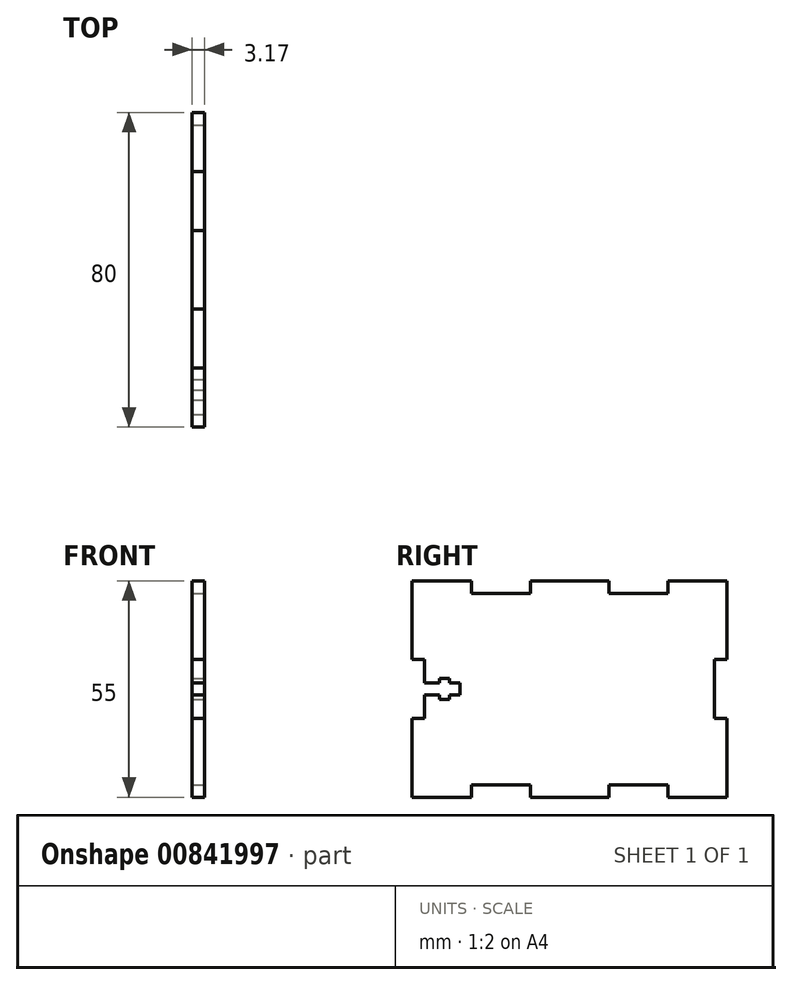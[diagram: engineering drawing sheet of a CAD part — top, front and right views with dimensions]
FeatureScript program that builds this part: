
annotation { "Feature Type Name" : "Feature", "Feature Type Description" : "" }
export const myFeature = defineFeature(function(context is Context, id is Id, definition is map)
    precondition{}
    {
        {
            assignVariable(context, id + "F0", {"name" : "mat_t", "anyValue" : 3.17});
        }
        {
            var Q0;
            Q0=qCreatedBy(makeId("Right.planeOp"),FACE);
            var sketch = newSketch(context, id + "F1", { "sketchPlane" : qUnion([Q0])});
            skLineSegment(sketch, "E0.bottom", {"start": v(40, -27.5) * mm, "end": v(-40, -27.5) * mm});
            skLineSegment(sketch, "E0.top", {"start": v(40, 27.5) * mm, "end": v(-40, 27.5) * mm});
            skLineSegment(sketch, "E0.left", {"start": v(40, -27.5) * mm, "end": v(40, 27.5) * mm});
            skLineSegment(sketch, "E0.right", {"start": v(-40, -27.5) * mm, "end": v(-40, 27.5) * mm});
            skPoint(sketch, "E0.middle", {"position": v(0, 0) * mm});
            skSolve(sketch);
        }
        {
            var Q0;
            Q0 = qSketchRegion(id + "F1", true);
            extrude(context, id + "F2", {"entities" : qUnion([Q0]), "depth" : (getVariable(context, 'mat_t')) * mm, "offsetDistance" : 25 * mm});
        }
        {
            var Q0;
            Q0=makeQuery(id+"F2.opExtrude","CAP_FACE",FACE,{"disambiguationData":[OSD([sQuery(id+"F1.wireOp",EDGE,"E0.bottom"),sQuery(id+"F1.wireOp",EDGE,"E0.top"),sQuery(id+"F1.wireOp",EDGE,"E0.left"),sQuery(id+"F1.wireOp",EDGE,"E0.right")])],"isStart":false});
            var sketch = newSketch(context, id + "F3", { "sketchPlane" : qUnion([Q0])});
            skLineSegment(sketch, "E1", {"start": v(0, 27.5) * mm, "end": v(0, -27.5) * mm, "construction": true});
            skLineSegment(sketch, "E2.bottom", {"start": v(40, 7.5) * mm, "end": v(36.83, 7.5) * mm});
            skLineSegment(sketch, "E2.top", {"start": v(40, -7.5) * mm, "end": v(36.83, -7.5) * mm});
            skLineSegment(sketch, "E2.left", {"start": v(40, 7.5) * mm, "end": v(40, -7.5) * mm});
            skLineSegment(sketch, "E2.right", {"start": v(36.83, 7.5) * mm, "end": v(36.83, -7.5) * mm});
            skPoint(sketch, "E3", {"position": v(40, 0) * mm});
            skLineSegment(sketch, "E4", {"start": v(-40, 0) * mm, "end": v(40, 0) * mm, "construction": true});
            skLineSegment(sketch, "E5.bottom", {"start": v(-25, -27.5) * mm, "end": v(-10, -27.5) * mm});
            skLineSegment(sketch, "E5.top", {"start": v(-25, -24.32) * mm, "end": v(-10, -24.32) * mm});
            skLineSegment(sketch, "E5.left", {"start": v(-25, -27.5) * mm, "end": v(-25, -24.32) * mm});
            skLineSegment(sketch, "E5.right", {"start": v(-10, -27.5) * mm, "end": v(-10, -24.32) * mm});
            skLineSegment(sketch, "E6.MirrorCS", {"start": v(25, -27.5) * mm, "end": v(10, -27.5) * mm});
            skLineSegment(sketch, "E7.MirrorCS", {"start": v(25, -27.5) * mm, "end": v(25, -24.32) * mm});
            skLineSegment(sketch, "E8.MirrorCS", {"start": v(10, -27.5) * mm, "end": v(10, -24.32) * mm});
            skLineSegment(sketch, "E9.MirrorCS", {"start": v(25, -24.32) * mm, "end": v(10, -24.32) * mm});
            skLineSegment(sketch, "E10", {"start": v(-17.5, -24.32) * mm, "end": v(-17.5, -27.5) * mm, "construction": true});
            skLineSegment(sketch, "E11", {"start": v(17.5, -24.32) * mm, "end": v(17.5, -27.5) * mm, "construction": true});
            skLineSegment(sketch, "E12.MirrorCS", {"start": v(17.5, 24.33) * mm, "end": v(17.5, 27.5) * mm, "construction": true});
            skLineSegment(sketch, "E13.MirrorCS", {"start": v(-10, 27.5) * mm, "end": v(-10, 24.32) * mm});
            skLineSegment(sketch, "E14.MirrorCS", {"start": v(-25, 24.32) * mm, "end": v(-10, 24.32) * mm});
            skLineSegment(sketch, "E15.MirrorCS", {"start": v(25, 24.33) * mm, "end": v(10, 24.32) * mm});
            skLineSegment(sketch, "E16.MirrorCS", {"start": v(10, 27.5) * mm, "end": v(10, 24.32) * mm});
            skLineSegment(sketch, "E17.MirrorCS", {"start": v(-25, 27.5) * mm, "end": v(-10, 27.5) * mm});
            skLineSegment(sketch, "E18.MirrorCS", {"start": v(25, 27.5) * mm, "end": v(25, 24.32) * mm});
            skLineSegment(sketch, "E19.MirrorCS", {"start": v(25, 27.5) * mm, "end": v(10, 27.5) * mm});
            skLineSegment(sketch, "E20.MirrorCS", {"start": v(-17.5, 24.32) * mm, "end": v(-17.5, 27.5) * mm, "construction": true});
            skLineSegment(sketch, "E21.MirrorCS", {"start": v(-25, 27.5) * mm, "end": v(-25, 24.32) * mm});
            skLineSegment(sketch, "E22.bottom", {"start": v(-36.82, -1.55) * mm, "end": v(-27.82, -1.55) * mm});
            skLineSegment(sketch, "E22.top", {"start": v(-36.82, 1.55) * mm, "end": v(-27.82, 1.55) * mm});
            skLineSegment(sketch, "E22.left", {"start": v(-36.82, -1.55) * mm, "end": v(-36.82, 1.55) * mm});
            skLineSegment(sketch, "E22.right", {"start": v(-27.82, -1.55) * mm, "end": v(-27.82, 1.55) * mm});
            skLineSegment(sketch, "E23", {"start": v(-36.83, 0) * mm, "end": v(-27.82, 0) * mm, "construction": true});
            skLineSegment(sketch, "E24.bottom", {"start": v(-30.58, -2.65) * mm, "end": v(-33.08, -2.65) * mm});
            skLineSegment(sketch, "E24.top", {"start": v(-30.58, 2.65) * mm, "end": v(-33.08, 2.65) * mm});
            skLineSegment(sketch, "E24.left", {"start": v(-30.58, -2.65) * mm, "end": v(-30.58, 2.65) * mm});
            skLineSegment(sketch, "E24.right", {"start": v(-33.08, -2.65) * mm, "end": v(-33.08, 2.65) * mm});
            skPoint(sketch, "E24.middle", {"position": v(-31.83, 0) * mm});
            skLineSegment(sketch, "E25.MirrorCS", {"start": v(-36.83, 7.5) * mm, "end": v(-36.83, -7.5) * mm});
            skPoint(sketch, "E26.MirrorP", {"position": v(-40, 0) * mm});
            skLineSegment(sketch, "E27.MirrorCS", {"start": v(-40, -7.5) * mm, "end": v(-36.83, -7.5) * mm});
            skLineSegment(sketch, "E28.MirrorCS", {"start": v(-40, 7.5) * mm, "end": v(-36.83, 7.5) * mm});
            skLineSegment(sketch, "E29.MirrorCS", {"start": v(-40, 7.5) * mm, "end": v(-40, -7.5) * mm});
            skPoint(sketch, "E30", {"position": v(-36.83, 0) * mm});
            skSolve(sketch);
        }
        {
            var Q0;
            Q0 = qSketchRegion(id + "F3", true);
            extrude(context, id + "F4", {"entities" : qUnion([Q0]), "operationType" : NewBodyOperationType.REMOVE, "endBound" : BoundingType.THROUGH_ALL, "oppositeDirection" : true, "depth" : 25 * mm, "offsetDistance" : 25 * mm});
        }
    });
